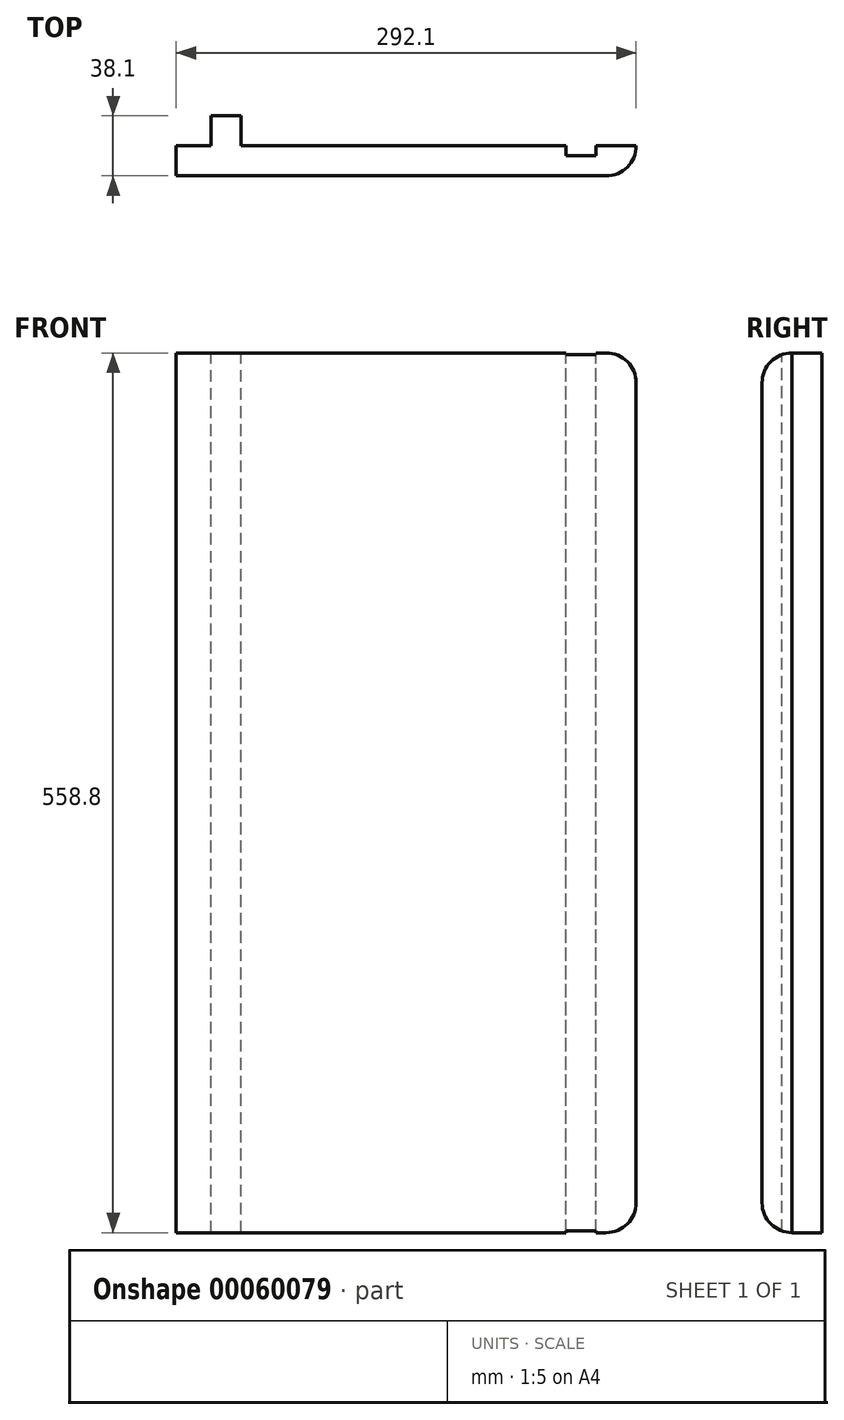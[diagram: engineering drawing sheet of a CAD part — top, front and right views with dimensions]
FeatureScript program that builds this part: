
annotation { "Feature Type Name" : "Feature", "Feature Type Description" : "" }
export const myFeature = defineFeature(function(context is Context, id is Id, definition is map)
    precondition{}
    {
        {
            var Q0;
            Q0=qCreatedBy(makeId("Front.planeOp"),FACE);
            var sketch = newSketch(context, id + "F0", { "sketchPlane" : qUnion([Q0])});
            skLineSegment(sketch, "E0.bottom", {"start": v(-146.05, -279.4) * mm, "end": v(146.05, -279.4) * mm});
            skLineSegment(sketch, "E0.top", {"start": v(-146.05, 279.4) * mm, "end": v(146.05, 279.4) * mm});
            skLineSegment(sketch, "E0.left", {"start": v(-146.05, -279.4) * mm, "end": v(-146.05, 279.4) * mm});
            skLineSegment(sketch, "E0.right", {"start": v(146.05, -279.4) * mm, "end": v(146.05, 279.4) * mm});
            skLineSegment(sketch, "E1", {"start": v(-146.05, 279.4) * mm, "end": v(146.05, -279.4) * mm, "construction": true});
            skSolve(sketch);
        }
        {
            var Q0;
            Q0=qSketchRegion(id+"F0",true);
            extrude(context, id + "F1", {"entities" : qUnion([Q0]), "oppositeDirection" : true, "depth" : 19.05 * mm});
        }
        {
            var Q0;
            Q0=makeQuery(id+"F1.opExtrude","CAP_FACE",FACE,{"disambiguationData":[OSD([sQuery(id+"F0.wireOp",EDGE,"E0.bottom"),sQuery(id+"F0.wireOp",EDGE,"E0.top"),sQuery(id+"F0.wireOp",EDGE,"E0.left"),sQuery(id+"F0.wireOp",EDGE,"E0.right")])],"isStart":false});
            var sketch = newSketch(context, id + "F3", { "sketchPlane" : qUnion([Q0])});
            skLineSegment(sketch, "E2.bottom", {"start": v(-120.65, -279.4) * mm, "end": v(-101.6, -279.4) * mm});
            skLineSegment(sketch, "E2.top", {"start": v(-120.65, 279.4) * mm, "end": v(-101.6, 279.4) * mm});
            skLineSegment(sketch, "E2.left", {"start": v(-120.65, -279.4) * mm, "end": v(-120.65, 279.4) * mm});
            skLineSegment(sketch, "E2.right", {"start": v(-101.6, -279.4) * mm, "end": v(-101.6, 279.4) * mm});
            skSolve(sketch);
        }
        {
            var Q0;
            Q0 = qSketchRegion(id + "F3", true);
            extrude(context, id + "F4", {"entities" : qUnion([Q0]), "operationType" : NewBodyOperationType.REMOVE, "oppositeDirection" : true, "depth" : 6.35 * mm});
        }
        {
            var Q0;
            Q0=makeQuery(id+"F1.opExtrude","CAP_EDGE",EDGE,{"disambiguationData":[OSD([sQuery(id+"F0.wireOp",EDGE,"E0.bottom")])],"isStart":true});
            var Q1;
            Q1=makeQuery(id+"F1.opExtrude","CAP_EDGE",EDGE,{"disambiguationData":[OSD([sQuery(id+"F0.wireOp",EDGE,"E0.right")])],"isStart":true});
            var Q2;
            Q2=makeQuery(id+"F1.opExtrude","CAP_EDGE",EDGE,{"disambiguationData":[OSD([sQuery(id+"F0.wireOp",EDGE,"E0.top")])],"isStart":true});
            var Q3;
            Q3=makeQuery(id+"F1.opExtrude","SWEPT_EDGE",EDGE,{"disambiguationData":[OSD([sQuery(id+"F0.wireOp",EDGE,"E0.bottom"),sQuery(id+"F0.wireOp",EDGE,"E0.right")])]});
            var Q4;
            Q4=makeQuery(id+"F1.opExtrude","SWEPT_EDGE",EDGE,{"disambiguationData":[OSD([sQuery(id+"F0.wireOp",EDGE,"E0.top"),sQuery(id+"F0.wireOp",EDGE,"E0.right")])]});
            fillet(context, id + "F5", {"entities" : qUnion([Q0, Q1, Q2, Q3, Q4]), "radius" : 19.05 * mm, "allowEdgeOverflow" : false});
        }
        {
            var Q0;
            {var subQ0=sQuery(id+"F0.wireOp",EDGE,"E0.bottom");var subQ1=sQuery(id+"F0.wireOp",EDGE,"E0.top");var subQ2=sQuery(id+"F0.wireOp",EDGE,"E0.left");Q0=makeQuery(id+"F4.boolean.opBoolean","SPLIT",FACE,{"disambiguationData":[TD([makeQuery(id+"F1.opExtrude","SWEPT_FACE",FACE,{"disambiguationData":[OSD([subQ2])]})])],"derivedFrom":makeQuery(id+"F1.opExtrude","CAP_FACE",FACE,{"disambiguationData":[OSD([subQ0,subQ1,subQ2,sQuery(id+"F0.wireOp",EDGE,"E0.right")])],"isStart":false})});}
            var sketch = newSketch(context, id + "F6", { "sketchPlane" : qUnion([Q0])});
            skLineSegment(sketch, "E3.bottom", {"start": v(123.83, -279.4) * mm, "end": v(104.78, -279.4) * mm});
            skLineSegment(sketch, "E3.top", {"start": v(123.82, 279.4) * mm, "end": v(104.77, 279.4) * mm});
            skLineSegment(sketch, "E3.left", {"start": v(123.83, -279.4) * mm, "end": v(123.82, 279.4) * mm});
            skLineSegment(sketch, "E3.right", {"start": v(104.78, -279.4) * mm, "end": v(104.77, 279.4) * mm});
            skSolve(sketch);
        }
        {
            var Q0;
            Q0 = qSketchRegion(id + "F6", true);
            extrude(context, id + "F7", {"entities" : qUnion([Q0]), "operationType" : NewBodyOperationType.ADD, "depth" : 19.05 * mm});
        }
    });
